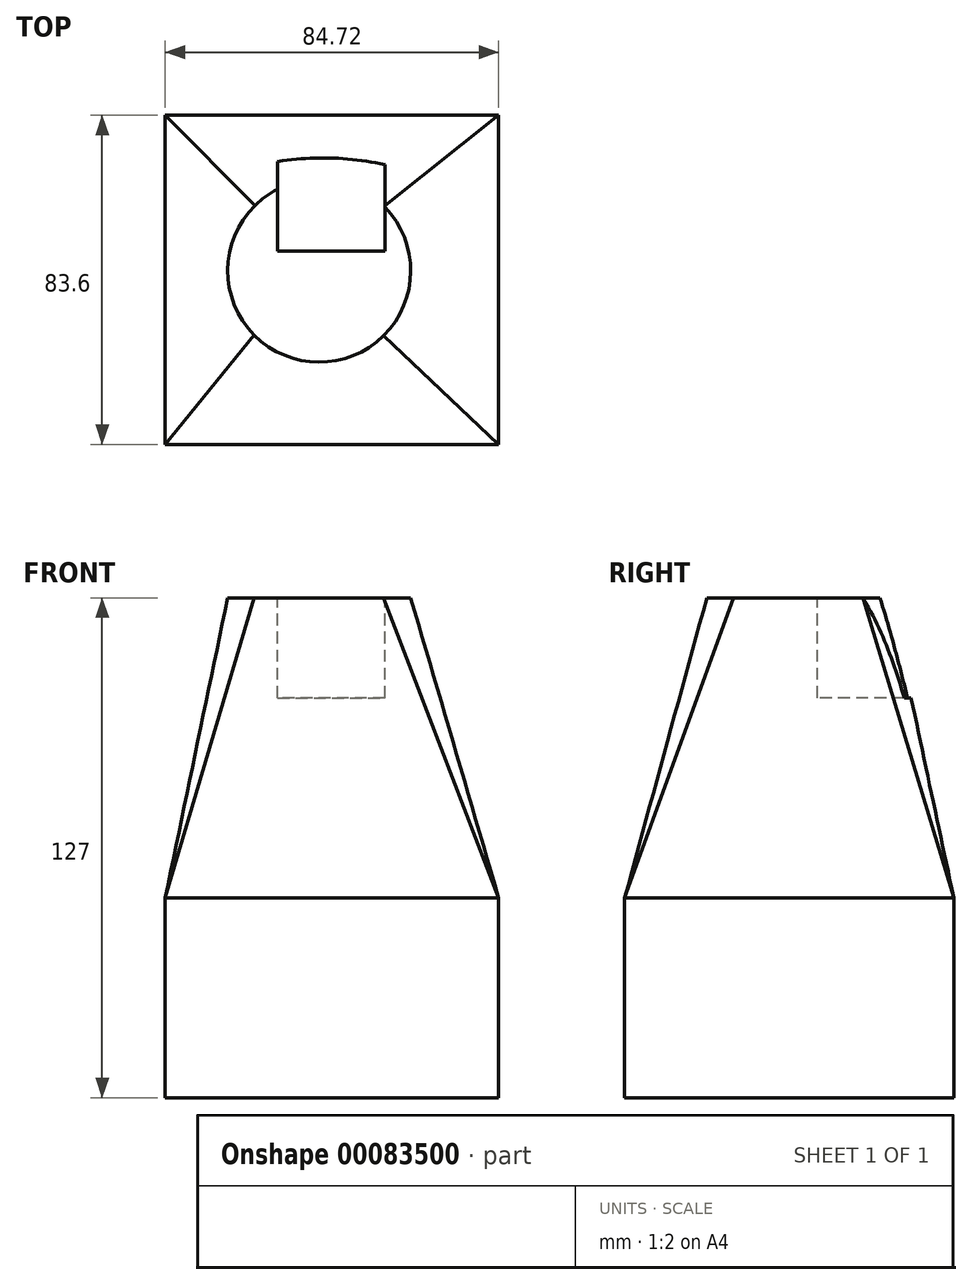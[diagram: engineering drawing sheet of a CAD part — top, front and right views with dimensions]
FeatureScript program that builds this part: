
annotation { "Feature Type Name" : "Feature", "Feature Type Description" : "" }
export const myFeature = defineFeature(function(context is Context, id is Id, definition is map)
    precondition{}
    {
        {
            var Q0;
            Q0=qCreatedBy(makeId("Top.planeOp"),FACE);
            var sketch = newSketch(context, id + "F0", { "sketchPlane" : qUnion([Q0])});
            skLineSegment(sketch, "E0.bottom", {"start": v(-37.81, 39.49) * mm, "end": v(46.9, 39.49) * mm});
            skLineSegment(sketch, "E0.top", {"start": v(-37.81, -44.11) * mm, "end": v(46.9, -44.11) * mm});
            skLineSegment(sketch, "E0.left", {"start": v(-37.81, 39.49) * mm, "end": v(-37.81, -44.11) * mm});
            skLineSegment(sketch, "E0.right", {"start": v(46.9, 39.49) * mm, "end": v(46.9, -44.11) * mm});
            skSolve(sketch);
        }
        {
            var Q0;
            Q0 = qSketchRegion(id + "F0", true);
            extrude(context, id + "F1", {"entities" : qUnion([Q0]), "depth" : 25.4 * mm});
        }
        {
            var Q0;
            Q0=makeQuery(id+"F1.opExtrude","CAP_FACE",FACE,{"disambiguationData":[OSD([sQuery(id+"F0.wireOp",EDGE,"E0.bottom"),sQuery(id+"F0.wireOp",EDGE,"E0.top"),sQuery(id+"F0.wireOp",EDGE,"E0.left"),sQuery(id+"F0.wireOp",EDGE,"E0.right")])],"isStart":false});
            extrude(context, id + "F2", {"entities" : qUnion([Q0]), "operationType" : NewBodyOperationType.ADD, "depth" : 25.4 * mm});
        }
        {
            var Q0;
            Q0=makeQuery(id+"F2.opExtrude","CAP_FACE",FACE,{"disambiguationData":[OSD([sQuery(id+"F0.wireOp",EDGE,"E0.bottom"),sQuery(id+"F0.wireOp",EDGE,"E0.top"),sQuery(id+"F0.wireOp",EDGE,"E0.left"),sQuery(id+"F0.wireOp",EDGE,"E0.right")])],"isStart":false});
            cPlane(context, id + "F3", {"entities" : qUnion([Q0]), "cplaneType" : CPlaneType.OFFSET, "offset" : 76.2 * mm, "width" : 152.4 * mm, "height" : 152.4 * mm});
        }
        {
            var Q0;
            Q0=qCreatedBy(id+"F3.planeOp",FACE);
            var sketch = newSketch(context, id + "F4", { "sketchPlane" : qUnion([Q0])});
            skCircle(sketch, "E1", {"center": v(1.3, 0) * mm, "radius": 23.24 * mm});
            skSolve(sketch);
        }
        {
            var Q1;
            Q1=makeQuery(id+"F2.opExtrude","CAP_FACE",FACE,{"disambiguationData":[OSD([sQuery(id+"F0.wireOp",EDGE,"E0.bottom"),sQuery(id+"F0.wireOp",EDGE,"E0.top"),sQuery(id+"F0.wireOp",EDGE,"E0.left"),sQuery(id+"F0.wireOp",EDGE,"E0.right")])],"isStart":false});
            var Q2;
            Q2=makeQuery(id+"F4.imprint","IMPRINT",FACE,{"disambiguationData":[TD([[makeQuery(id+"F4.imprint","IMPRINT",EDGE,{"derivedFrom":sQuery(id+"F4.wireOp",EDGE,"E1")}),1.0]])]});
            loft(context, id + "F5", {"operationType" : NewBodyOperationType.ADD, "sheetProfilesArray" : [{ "sheetProfileEntities" : qUnion([Q1]) }, { "sheetProfileEntities" : qUnion([Q2]) }]});
        }
        {
            var Q0;
            Q0=makeQuery(id+"F5.opLoft","CAP_FACE",FACE,{"disambiguationData":[OSD([makeQuery(id+"F4.imprint","IMPRINT",FACE,{"disambiguationData":[TD([[makeQuery(id+"F4.imprint","IMPRINT",EDGE,{"derivedFrom":sQuery(id+"F4.wireOp",EDGE,"E1")}),1.0]])]})])],"isStart":true});
            var sketch = newSketch(context, id + "F6", { "sketchPlane" : qUnion([Q0])});
            skLineSegment(sketch, "E2.bottom", {"start": v(17.98, 39.69) * mm, "end": v(-9.24, 39.69) * mm});
            skLineSegment(sketch, "E2.top", {"start": v(17.98, 4.92) * mm, "end": v(-9.24, 4.92) * mm});
            skLineSegment(sketch, "E2.left", {"start": v(17.98, 39.69) * mm, "end": v(17.98, 4.92) * mm});
            skLineSegment(sketch, "E2.right", {"start": v(-9.24, 39.69) * mm, "end": v(-9.24, 4.92) * mm});
            skSolve(sketch);
        }
        {
            var Q0;
            {var subQ1=sQuery(id+"F6.wireOp",EDGE,"E2.top");Q0=makeQuery(id+"F6.imprint","IMPRINT",FACE,{"disambiguationData":[TD([[makeQuery(id+"F6.imprint","IMPRINT",EDGE,{"derivedFrom":subQ1}),-1.0]])]});}
            var Q1;
            {var subQ9=sQuery(id+"F6.wireOp",EDGE,"E2.bottom");Q1=makeQuery(id+"F6.imprint","IMPRINT",FACE,{"disambiguationData":[TD([[makeQuery(id+"F6.imprint","IMPRINT",EDGE,{"derivedFrom":subQ9}),1.0]])]});}
            extrude(context, id + "F7", {"entities" : qUnion([Q0, Q1]), "operationType" : NewBodyOperationType.REMOVE, "oppositeDirection" : true, "depth" : 25.4 * mm});
        }
    });
